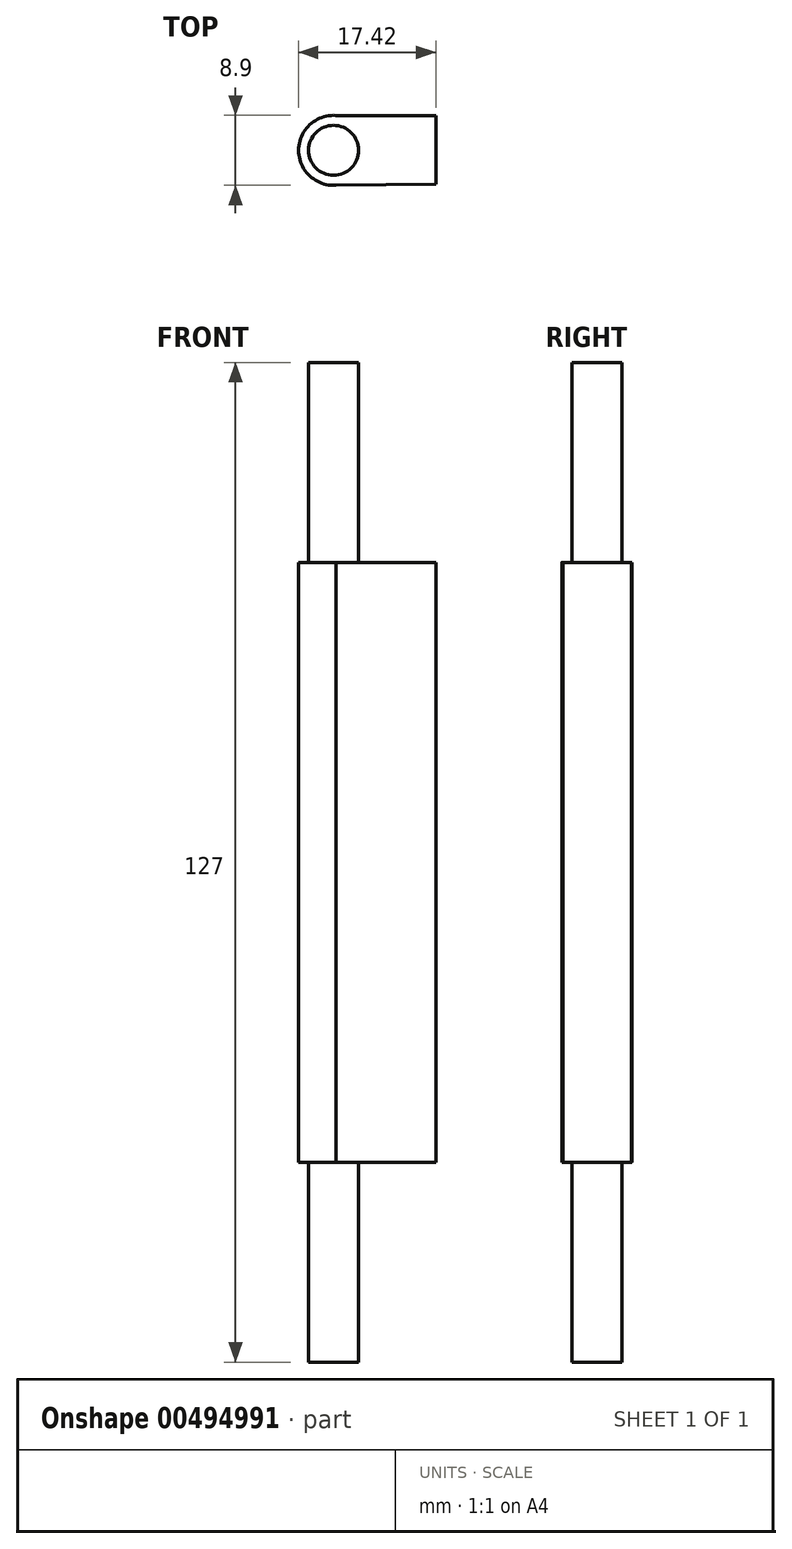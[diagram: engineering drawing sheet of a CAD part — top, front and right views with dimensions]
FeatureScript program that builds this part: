
annotation { "Feature Type Name" : "Feature", "Feature Type Description" : "" }
export const myFeature = defineFeature(function(context is Context, id is Id, definition is map)
    precondition{}
    {
        {
            var Q0;
            Q0=qCreatedBy(makeId("Top.planeOp"),FACE);
            var sketch = newSketch(context, id + "F0", { "sketchPlane" : qUnion([Q0])});
            skCircle(sketch, "E0", {"center": v(0, 0) * mm, "radius": 3.18 * mm});
            skArc(sketch, "E1", {"start": v(0.28, 4.44) * mm, "mid": v(-4.45, 0) * mm, "end": v(0.28, -4.44) * mm});
            skLineSegment(sketch, "E2", {"start": v(0.28, 4.44) * mm, "end": v(12.98, 4.44) * mm});
            skLineSegment(sketch, "E3", {"start": v(12.98, 4.44) * mm, "end": v(12.98, -4.28) * mm});
            skLineSegment(sketch, "E4", {"start": v(0.28, -4.44) * mm, "end": v(12.98, -4.28) * mm});
            skSolve(sketch);
        }
        {
            var Q0;
            Q0=makeQuery(id+"F0.imprint","IMPRINT",FACE,{"disambiguationData":[TD([[makeQuery(id+"F0.imprint","IMPRINT",EDGE,{"derivedFrom":sQuery(id+"F0.wireOp",EDGE,"E0")}),1.0]])]});
            extrude(context, id + "F1", {"entities" : qUnion([Q0]), "endBound" : BoundingType.SYMMETRIC, "depth" : 127 * mm});
        }
        {
            var Q0;
            Q0=makeQuery(id+"F0.imprint","IMPRINT",FACE,{"disambiguationData":[TD([[makeQuery(id+"F0.imprint","IMPRINT",EDGE,{"derivedFrom":sQuery(id+"F0.wireOp",EDGE,"E0")}),-1.0]])]});
            extrude(context, id + "F2", {"entities" : qUnion([Q0]), "operationType" : NewBodyOperationType.ADD, "endBound" : BoundingType.SYMMETRIC, "depth" : 76.2 * mm});
        }
    });
